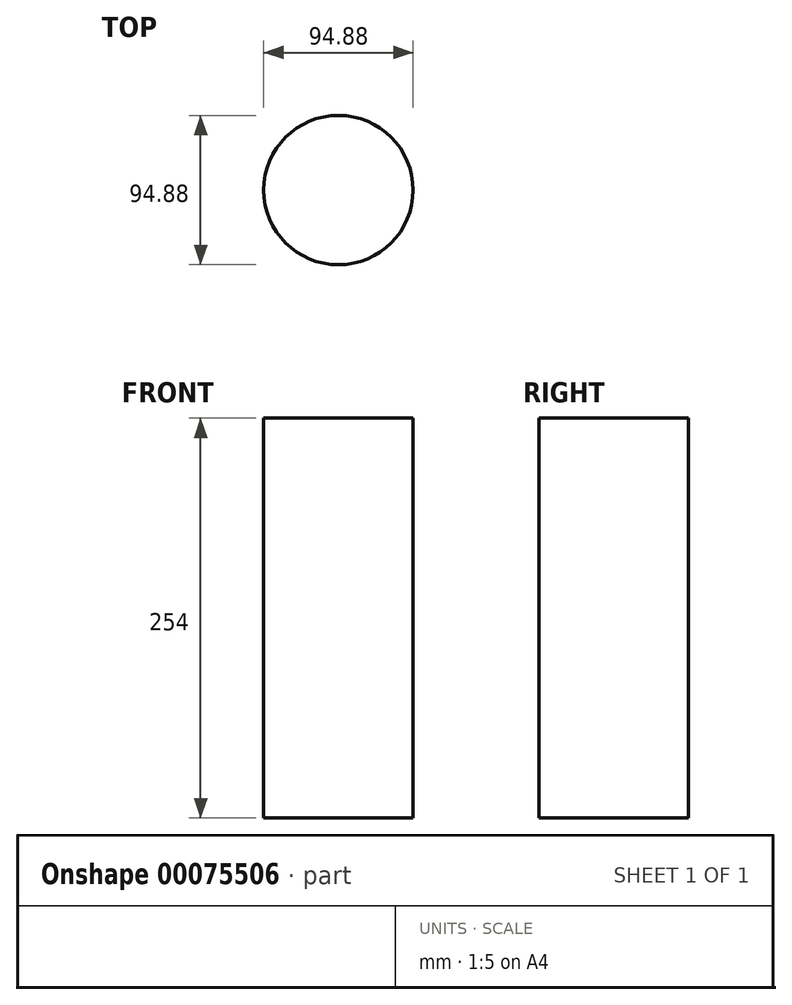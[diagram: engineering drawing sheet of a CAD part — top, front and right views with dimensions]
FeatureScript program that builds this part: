
annotation { "Feature Type Name" : "Feature", "Feature Type Description" : "" }
export const myFeature = defineFeature(function(context is Context, id is Id, definition is map)
    precondition{}
    {
        {
            var Q0;
            Q0=qCreatedBy(makeId("Top.planeOp"),FACE);
            var sketch = newSketch(context, id + "F0", { "sketchPlane" : qUnion([Q0])});
            skCircle(sketch, "E0", {"center": v(0, 0) * mm, "radius": 47.44 * mm});
            skSolve(sketch);
        }
        {
            var Q0;
            Q0 = qSketchRegion(id + "F0", true);
            extrude(context, id + "F1", {"entities" : qUnion([Q0]), "depth" : 254 * mm});
        }
    });
